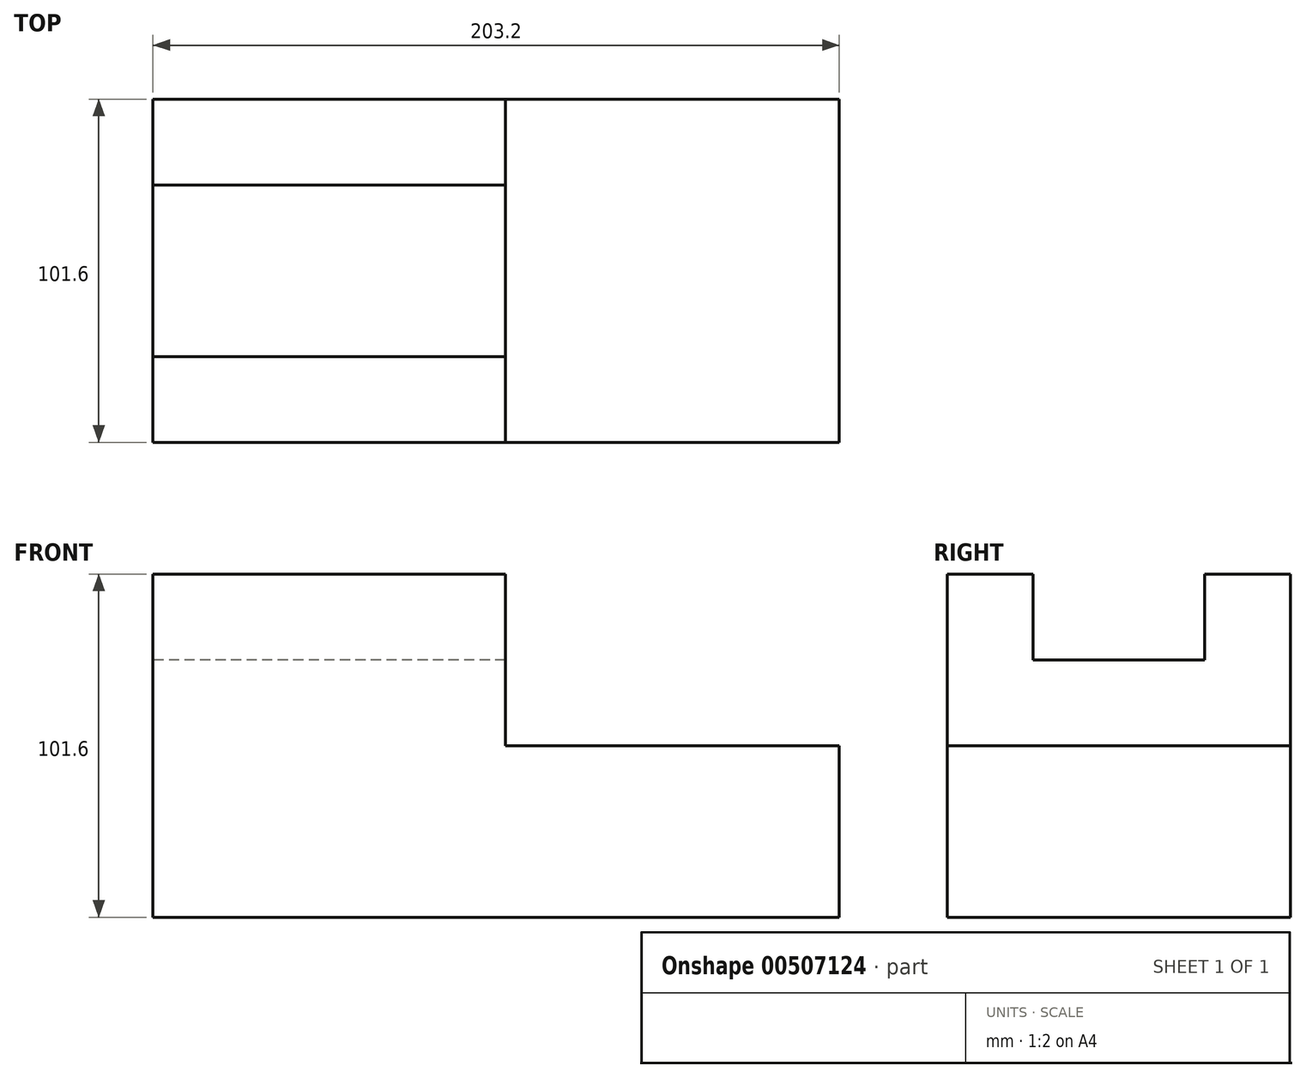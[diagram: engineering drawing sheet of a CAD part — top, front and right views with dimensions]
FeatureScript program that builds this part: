
annotation { "Feature Type Name" : "Feature", "Feature Type Description" : "" }
export const myFeature = defineFeature(function(context is Context, id is Id, definition is map)
    precondition{}
    {
        {
            var Q0;
            Q0=qCreatedBy(makeId("Front.planeOp"),FACE);
            var sketch = newSketch(context, id + "F0", { "sketchPlane" : qUnion([Q0])});
            skLineSegment(sketch, "E0.bottom", {"start": v(-77.14, -8.02) * mm, "end": v(27.2, -8.02) * mm});
            skLineSegment(sketch, "E0.top", {"start": v(-77.14, -109.62) * mm, "end": v(126.06, -109.62) * mm});
            skLineSegment(sketch, "E0.left", {"start": v(-77.14, -8.02) * mm, "end": v(-77.14, -109.62) * mm});
            skLineSegment(sketch, "E0.right", {"start": v(126.06, -58.82) * mm, "end": v(126.06, -109.62) * mm});
            skLineSegment(sketch, "E1.top", {"start": v(126.06, -58.82) * mm, "end": v(27.2, -58.82) * mm});
            skLineSegment(sketch, "E1.right", {"start": v(27.2, -8.02) * mm, "end": v(27.2, -58.82) * mm});
            skSolve(sketch);
        }
        {
            var Q0;
            Q0 = qSketchRegion(id + "F0", true);
            extrude(context, id + "F1", {"entities" : qUnion([Q0]), "depth" : 101.6 * mm});
        }
        {
            var Q0;
            Q0=qCreatedBy(makeId("Right.planeOp"),FACE);
            var sketch = newSketch(context, id + "F2", { "sketchPlane" : qUnion([Q0])});
            skLineSegment(sketch, "E2.bottom", {"start": v(-76.2, -8.02) * mm, "end": v(-25.4, -8.02) * mm});
            skLineSegment(sketch, "E2.top", {"start": v(-76.2, -33.42) * mm, "end": v(-25.4, -33.42) * mm});
            skLineSegment(sketch, "E2.left", {"start": v(-76.2, -8.02) * mm, "end": v(-76.2, -33.42) * mm});
            skLineSegment(sketch, "E2.right", {"start": v(-25.4, -8.02) * mm, "end": v(-25.4, -33.42) * mm});
            skSolve(sketch);
        }
        {
            var Q0;
            Q0 = qSketchRegion(id + "F2", true);
            extrude(context, id + "F3", {"entities" : qUnion([Q0]), "operationType" : NewBodyOperationType.REMOVE, "endBound" : BoundingType.THROUGH_ALL, "depth" : 203.2 * mm});
        }
        {
            var Q0;
            Q0=makeQuery(id+"F3.boolean.opBoolean","COPY",FACE,{"derivedFrom":makeQuery(id+"F3.opExtrude","CAP_FACE",FACE,{"disambiguationData":[OSD([sQuery(id+"F2.wireOp",EDGE,"E2.bottom"),sQuery(id+"F2.wireOp",EDGE,"E2.top"),sQuery(id+"F2.wireOp",EDGE,"E2.left"),sQuery(id+"F2.wireOp",EDGE,"E2.right")])],"isStart":true})});
            extrude(context, id + "F4", {"entities" : qUnion([Q0]), "operationType" : NewBodyOperationType.REMOVE, "endBound" : BoundingType.THROUGH_ALL, "oppositeDirection" : true, "depth" : 25.4 * mm});
        }
    });
